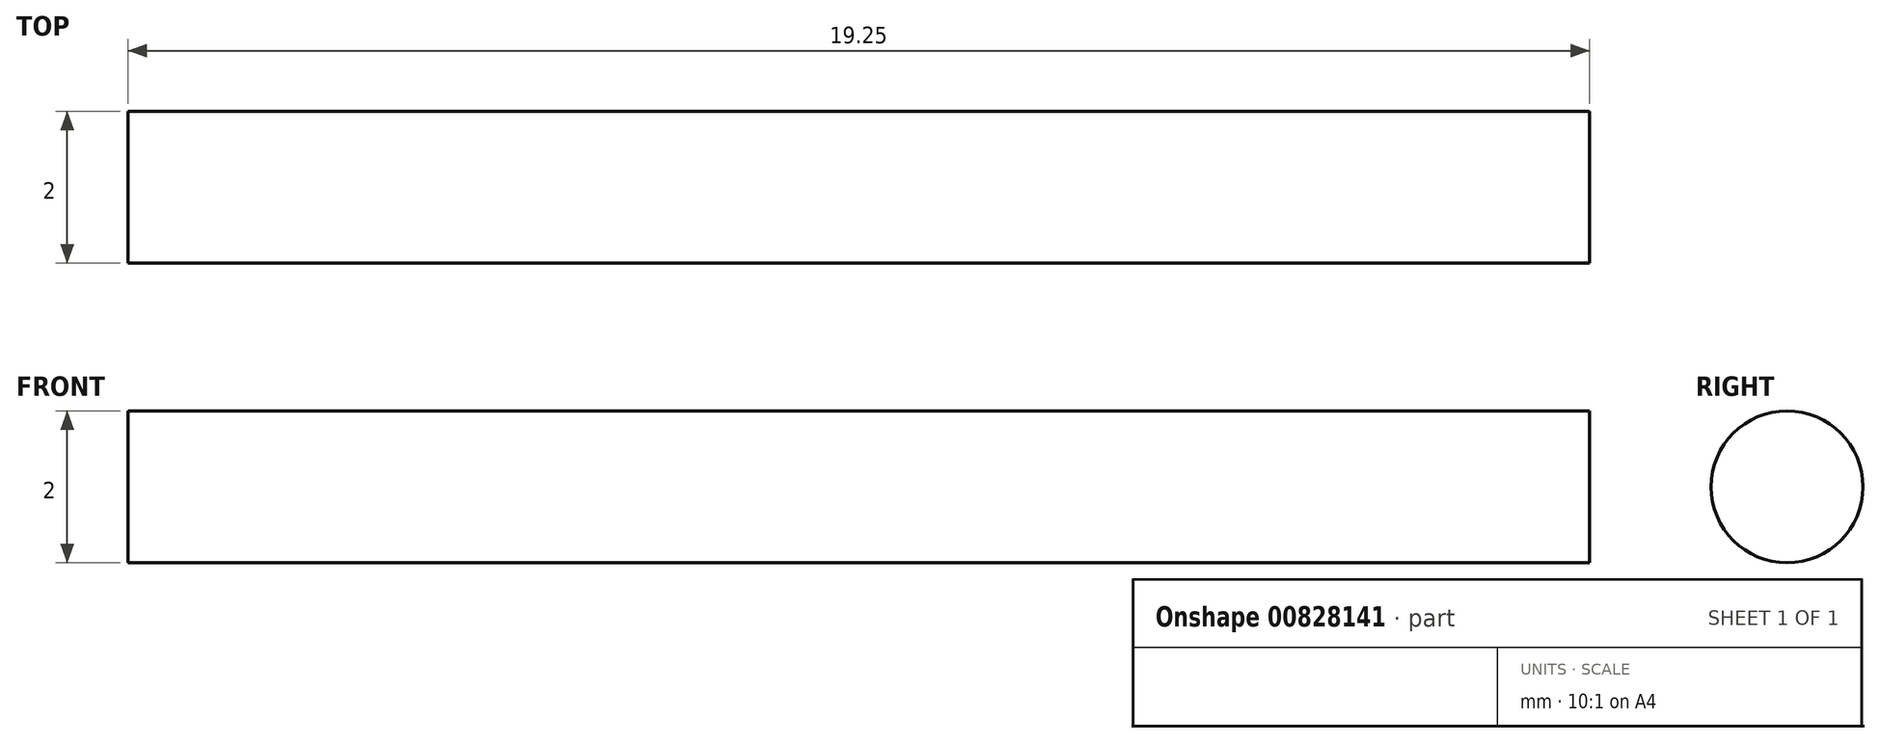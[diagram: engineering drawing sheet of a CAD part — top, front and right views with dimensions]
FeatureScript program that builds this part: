
annotation { "Feature Type Name" : "Feature", "Feature Type Description" : "" }
export const myFeature = defineFeature(function(context is Context, id is Id, definition is map)
    precondition{}
    {
        {
            var Q0;
            Q0=qCreatedBy(makeId("Front.planeOp"),FACE);
            var sketch = newSketch(context, id + "F0", { "sketchPlane" : qUnion([Q0])});
            skLineSegment(sketch, "E0.bottom", {"start": v(0, 0) * mm, "end": v(19.25, 0) * mm});
            skLineSegment(sketch, "E0.top", {"start": v(0, 1) * mm, "end": v(19.25, 1) * mm});
            skLineSegment(sketch, "E0.left", {"start": v(0, 0) * mm, "end": v(0, 1) * mm});
            skLineSegment(sketch, "E0.right", {"start": v(19.25, 0) * mm, "end": v(19.25, 1) * mm});
            skSolve(sketch);
        }
        {
            var Q0;
            Q0 = qSketchRegion(id + "F0", true);
            var Q1;
            Q1=sQuery(id+"F0.wireOp",EDGE,"E0.bottom");
            revolve(context, id + "F1", {"surfaceOperationType" : NewSurfaceOperationType.NEW, "entities" : qUnion([Q0]), "axis" : qUnion([Q1]), "revolveType" : RevolveType.FULL});
        }
    });
